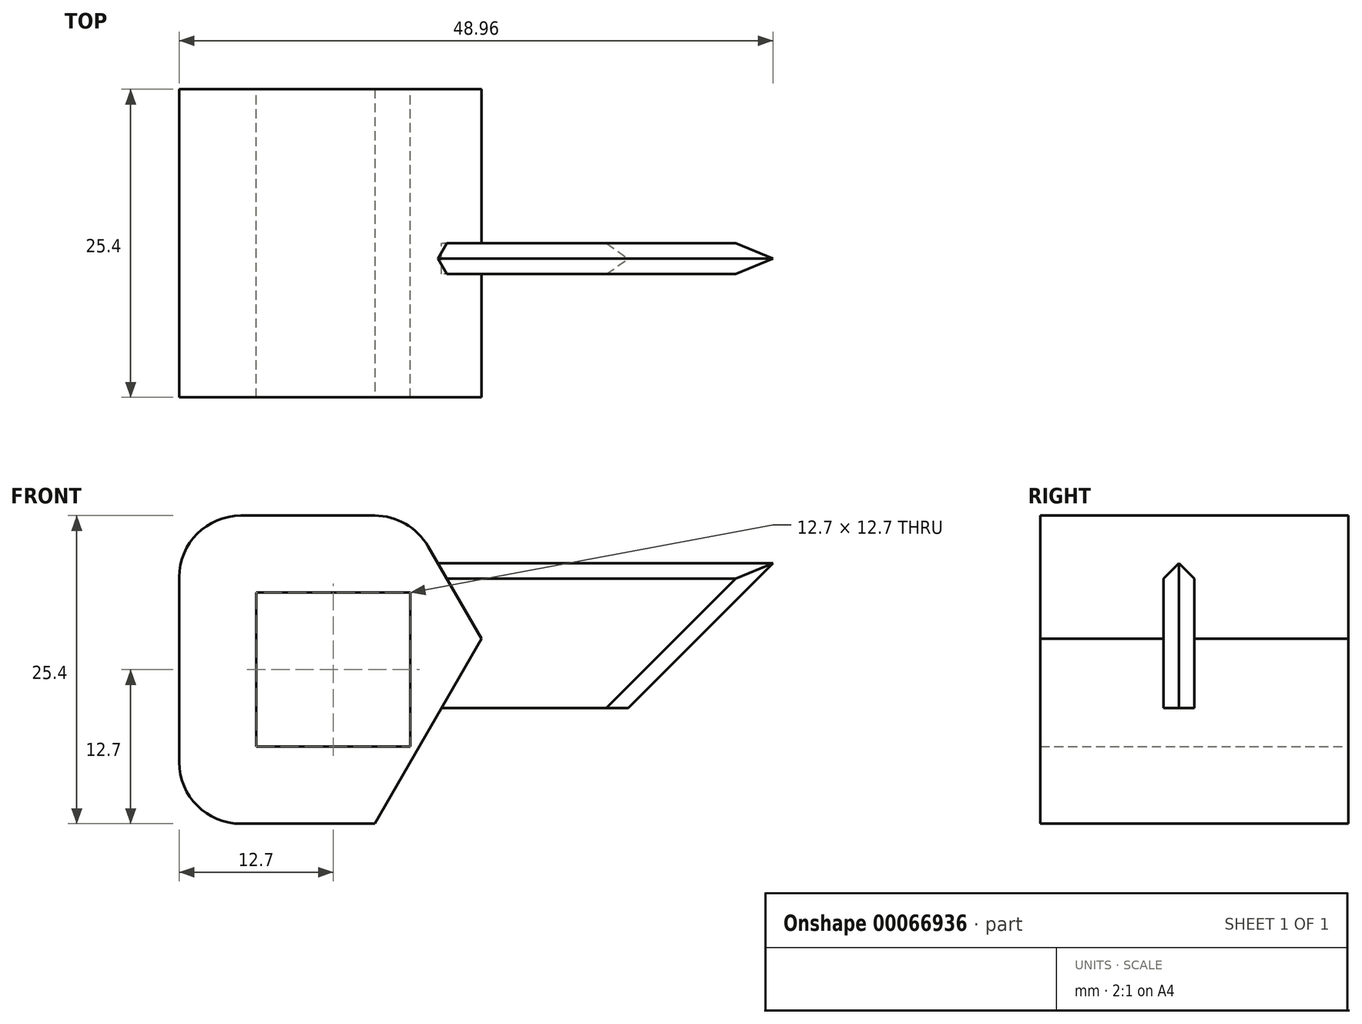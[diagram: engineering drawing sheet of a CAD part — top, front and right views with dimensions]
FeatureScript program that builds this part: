
annotation { "Feature Type Name" : "Feature", "Feature Type Description" : "" }
export const myFeature = defineFeature(function(context is Context, id is Id, definition is map)
    precondition{}
    {
        {
            var Q0;
            Q0=qCreatedBy(makeId("Front.planeOp"),FACE);
            var sketch = newSketch(context, id + "F0", { "sketchPlane" : qUnion([Q0])});
            skLineSegment(sketch, "E0.top", {"start": v(0, 25.4) * mm, "end": v(19.05, 25.4) * mm});
            skLineSegment(sketch, "E0.left", {"start": v(0, 0) * mm, "end": v(0, 25.4) * mm});
            skLineSegment(sketch, "E1.bottom", {"start": v(6.35, 6.35) * mm, "end": v(19.05, 6.35) * mm});
            skLineSegment(sketch, "E1.top", {"start": v(6.35, 19.05) * mm, "end": v(19.05, 19.05) * mm});
            skLineSegment(sketch, "E1.left", {"start": v(6.35, 6.35) * mm, "end": v(6.35, 19.05) * mm});
            skLineSegment(sketch, "E1.right", {"start": v(19.05, 6.35) * mm, "end": v(19.05, 19.05) * mm});
            skLineSegment(sketch, "E2", {"start": v(19.05, 25.4) * mm, "end": v(33.71, 0) * mm});
            skLineSegment(sketch, "E3", {"start": v(0, 0) * mm, "end": v(33.71, 0) * mm});
            skSolve(sketch);
        }
        {
            var Q0;
            Q0=makeQuery(id+"F0.imprint","IMPRINT",FACE,{"disambiguationData":[TD([[makeQuery(id+"F0.imprint","IMPRINT",EDGE,{"derivedFrom":sQuery(id+"F0.wireOp",EDGE,"E0.bottom")}),1.0]])]});
            var Q1;
            Q1=makeQuery(id+"F0.imprint","IMPRINT",FACE,{"disambiguationData":[TD([[makeQuery(id+"F0.imprint","IMPRINT",EDGE,{"derivedFrom":sQuery(id+"F0.wireOp",EDGE,"E0.top")}),-1.0]])]});
            extrude(context, id + "F1", {"entities" : qUnion([Q0, Q1]), "depth" : 25.4 * mm});
        }
        {
            var Q0;
            Q0=makeQuery(id+"F1.opExtrude","CAP_FACE",FACE,{"disambiguationData":[OSD([sQuery(id+"F0.wireOp",EDGE,"E0.bottom"),sQuery(id+"F0.wireOp",EDGE,"E0.top"),sQuery(id+"F0.wireOp",EDGE,"E0.left"),sQuery(id+"F0.wireOp",EDGE,"E1.bottom"),sQuery(id+"F0.wireOp",EDGE,"E1.top"),sQuery(id+"F0.wireOp",EDGE,"E1.left"),sQuery(id+"F0.wireOp",EDGE,"E1.right"),sQuery(id+"F0.wireOp",EDGE,"E2"),sQuery(id+"F0.wireOp",EDGE,"E3")])],"isStart":false});
            var Q1;
            Q1=makeQuery(id+"F1.opExtrude","CAP_FACE",FACE,{"disambiguationData":[OSD([sQuery(id+"F0.wireOp",EDGE,"E0.bottom"),sQuery(id+"F0.wireOp",EDGE,"E0.top"),sQuery(id+"F0.wireOp",EDGE,"E0.left"),sQuery(id+"F0.wireOp",EDGE,"E1.bottom"),sQuery(id+"F0.wireOp",EDGE,"E1.top"),sQuery(id+"F0.wireOp",EDGE,"E1.left"),sQuery(id+"F0.wireOp",EDGE,"E1.right"),sQuery(id+"F0.wireOp",EDGE,"E2"),sQuery(id+"F0.wireOp",EDGE,"E3")])],"isStart":true});
            cPlane(context, id + "F2", {"entities" : qUnion([Q0, Q1]), "cplaneType" : CPlaneType.MID_PLANE, "offset" : 152.4 * mm, "width" : 152.4 * mm, "height" : 152.4 * mm});
        }
        {
            var Q0;
            Q0=qCreatedBy(id+"F2.planeOp",FACE);
            var sketch = newSketch(context, id + "F3", { "sketchPlane" : qUnion([Q0])});
            skLineSegment(sketch, "E4", {"start": v(20.88, 22.23) * mm, "end": v(50.8, 22.23) * mm});
            skLineSegment(sketch, "E5", {"start": v(50.8, 22.23) * mm, "end": v(38.1, 9.53) * mm});
            skLineSegment(sketch, "E6", {"start": v(38.1, 9.53) * mm, "end": v(28.22, 9.53) * mm});
            skLineSegment(sketch, "E7", {"start": v(28.22, 9.53) * mm, "end": v(20.88, 22.23) * mm});
            skSolve(sketch);
        }
        {
            var Q0;
            Q0=makeQuery(id+"F3.imprint","IMPRINT",FACE,{"disambiguationData":[TD([[makeQuery(id+"F3.imprint","IMPRINT",EDGE,{"derivedFrom":sQuery(id+"F3.wireOp",EDGE,"E4")}),-1.0]])]});
            extrude(context, id + "F4", {"entities" : qUnion([Q0]), "operationType" : NewBodyOperationType.ADD, "depth" : 2.54 * mm});
        }
        {
            var Q0;
            Q0=makeQuery(id+"F1.opExtrude","SWEPT_EDGE",EDGE,{"disambiguationData":[OSD([sQuery(id+"F0.wireOp",EDGE,"E0.left"),sQuery(id+"F0.wireOp",EDGE,"E3")])]});
            var Q1;
            Q1=makeQuery(id+"F1.opExtrude","SWEPT_EDGE",EDGE,{"disambiguationData":[OSD([sQuery(id+"F0.wireOp",EDGE,"E0.top"),sQuery(id+"F0.wireOp",EDGE,"E0.left")])]});
            var Q2;
            Q2=makeQuery(id+"F1.opExtrude","SWEPT_EDGE",EDGE,{"disambiguationData":[OSD([sQuery(id+"F0.wireOp",EDGE,"E0.top"),sQuery(id+"F0.wireOp",EDGE,"E2")])]});
            fillet(context, id + "F5", {"entities" : qUnion([Q0, Q1, Q2]), "radius" : 5.08 * mm, "tangentPropagation" : true, "allowEdgeOverflow" : false});
        }
        {
            var Q0;
            Q0=makeQuery(id+"F1.opExtrude","SWEPT_EDGE",EDGE,{"disambiguationData":[OSD([sQuery(id+"F0.wireOp",EDGE,"E2"),sQuery(id+"F0.wireOp",EDGE,"E3")])]});
            chamfer(context, id + "F6", {"entities" : qUnion([Q0]), "width" : 10.16 * mm, "tangentPropagation" : true});
        }
        {
            var Q0;
            Q0=makeQuery(id+"F4.opExtrude","CAP_EDGE",EDGE,{"disambiguationData":[OSD([sQuery(id+"F3.wireOp",EDGE,"E4")])],"isStart":true});
            var Q1;
            Q1=makeQuery(id+"F4.opExtrude","CAP_EDGE",EDGE,{"disambiguationData":[OSD([sQuery(id+"F3.wireOp",EDGE,"E4")])],"isStart":false});
            chamfer(context, id + "F7", {"entities" : qUnion([Q0, Q1]), "width" : 2.03 * mm, "tangentPropagation" : true});
        }
        {
            var Q0;
            Q0=makeQuery(id+"F4.opExtrude","CAP_EDGE",EDGE,{"disambiguationData":[OSD([sQuery(id+"F3.wireOp",EDGE,"E5")])],"isStart":true});
            var Q1;
            Q1=makeQuery(id+"F4.opExtrude","CAP_EDGE",EDGE,{"disambiguationData":[OSD([sQuery(id+"F3.wireOp",EDGE,"E5")])],"isStart":false});
            chamfer(context, id + "F8", {"entities" : qUnion([Q0, Q1]), "width" : 2.03 * mm, "tangentPropagation" : true});
        }
    });
